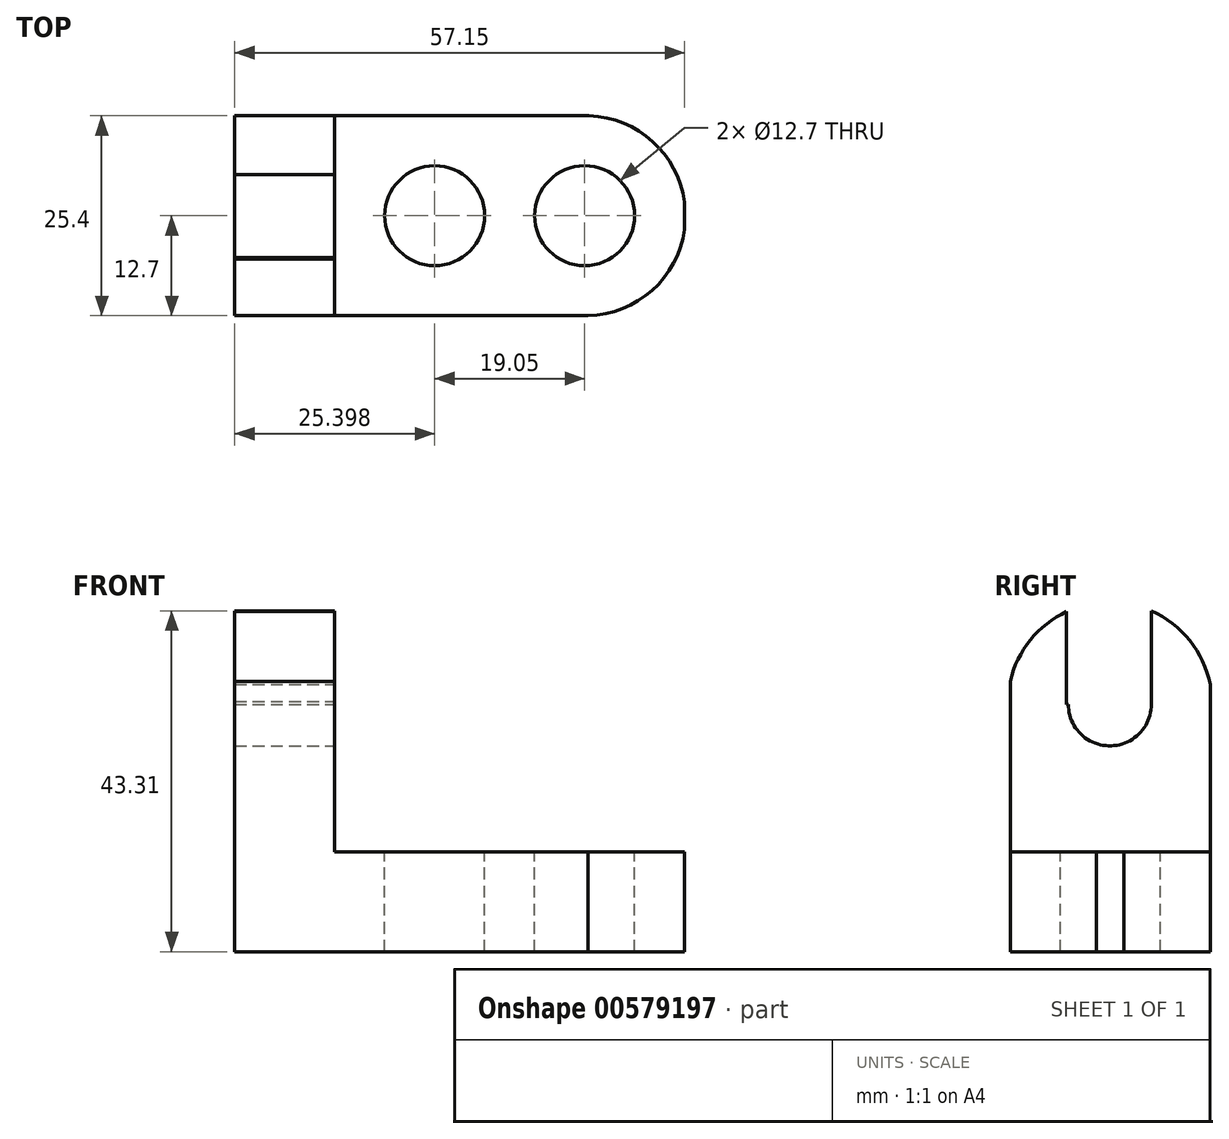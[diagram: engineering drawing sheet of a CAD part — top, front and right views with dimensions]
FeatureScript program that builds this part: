
annotation { "Feature Type Name" : "Feature", "Feature Type Description" : "" }
export const myFeature = defineFeature(function(context is Context, id is Id, definition is map)
    precondition{}
    {
        {
            var Q0;
            Q0=qCreatedBy(makeId("Front.planeOp"),FACE);
            var sketch = newSketch(context, id + "F0", { "sketchPlane" : qUnion([Q0])});
            skLineSegment(sketch, "E0", {"start": v(-58.37, 52.06) * mm, "end": v(-58.37, 7.61) * mm});
            skLineSegment(sketch, "E1", {"start": v(-58.37, 7.61) * mm, "end": v(-1.22, 7.61) * mm});
            skLineSegment(sketch, "E2", {"start": v(-1.22, 7.61) * mm, "end": v(-1.22, 20.31) * mm});
            skLineSegment(sketch, "E3", {"start": v(-1.22, 20.31) * mm, "end": v(-45.67, 20.31) * mm});
            skLineSegment(sketch, "E4", {"start": v(-45.67, 20.31) * mm, "end": v(-45.67, 52.06) * mm});
            skLineSegment(sketch, "E5", {"start": v(-45.67, 52.06) * mm, "end": v(-58.37, 52.06) * mm});
            skSolve(sketch);
        }
        {
            var Q0;
            Q0=makeQuery(id+"F0.imprint","IMPRINT",FACE,{"disambiguationData":[TD([[makeQuery(id+"F0.imprint","IMPRINT",EDGE,{"derivedFrom":sQuery(id+"F0.wireOp",EDGE,"E0")}),1.0]])]});
            extrude(context, id + "F1", {"entities" : qUnion([Q0]), "depth" : 25.4 * mm, "offsetDistance" : 25.4 * mm});
        }
        {
            var Q0;
            Q0=makeQuery(id+"F1.opExtrude","SWEPT_FACE",FACE,{"disambiguationData":[OSD([sQuery(id+"F0.wireOp",EDGE,"E3")])]});
            var sketch = newSketch(context, id + "F2", { "sketchPlane" : qUnion([Q0])});
            skCircle(sketch, "E6", {"center": v(-32.97, -12.7) * mm, "radius": 6.35 * mm});
            skCircle(sketch, "E7", {"center": v(-13.92, -12.7) * mm, "radius": 6.35 * mm});
            skSolve(sketch);
        }
        {
            var Q0;
            Q0=makeQuery(id+"F2.imprint","IMPRINT",FACE,{"disambiguationData":[TD([[makeQuery(id+"F2.imprint","IMPRINT",EDGE,{"derivedFrom":sQuery(id+"F2.wireOp",EDGE,"E6")}),1.0]])]});
            var Q1;
            Q1=makeQuery(id+"F2.imprint","IMPRINT",FACE,{"disambiguationData":[TD([[makeQuery(id+"F2.imprint","IMPRINT",EDGE,{"derivedFrom":sQuery(id+"F2.wireOp",EDGE,"E7")}),1.0]])]});
            extrude(context, id + "F3", {"entities" : qUnion([Q0, Q1]), "operationType" : NewBodyOperationType.REMOVE, "endBound" : BoundingType.THROUGH_ALL, "oppositeDirection" : true, "depth" : 25.4 * mm, "offsetDistance" : 25.4 * mm});
        }
        {
            var Q0;
            Q0=makeQuery(id+"F1.opExtrude","SWEPT_FACE",FACE,{"disambiguationData":[OSD([sQuery(id+"F0.wireOp",EDGE,"E3")])]});
            var sketch = newSketch(context, id + "F4", { "sketchPlane" : qUnion([Q0])});
            skArc(sketch, "E8", {"start": v(-14.1, -25.4) * mm, "mid": v(-1.1, -13.08) * mm, "end": v(-13.34, 0) * mm});
            skSolve(sketch);
        }
        {
            var Q0;
            {var subQ0=sQuery(id+"F4.wireOp",EDGE,"E8");var subQ1=sQuery(id+"F0.wireOp",EDGE,"E3");var subQ2=makeQuery(id+"F1.opExtrude","CAP_EDGE",EDGE,{"disambiguationData":[OSD([subQ1])],"isStart":true});var subQ3=makeQuery(id+"F4.imprint","INTERSECT",VERTEX,{"derivedFrom":[subQ2,subQ0]});Q0=makeQuery(id+"F4.imprint","IMPRINT",FACE,{"disambiguationData":[TD([[makeQuery(id+"F4.imprint","IMPRINT",EDGE,{"disambiguationData":[TD([[subQ3,1.0]])],"derivedFrom":subQ0}),-1.0]])]});}
            var Q1;
            {var subQ0=sQuery(id+"F4.wireOp",EDGE,"E8");var subQ1=sQuery(id+"F0.wireOp",EDGE,"E3");var subQ2=makeQuery(id+"F1.opExtrude","CAP_EDGE",EDGE,{"disambiguationData":[OSD([subQ1])],"isStart":false});var subQ3=makeQuery(id+"F4.imprint","INTERSECT",VERTEX,{"disambiguationData":[OD(1.0)],"derivedFrom":[subQ2,subQ0]});Q1=makeQuery(id+"F4.imprint","IMPRINT",FACE,{"disambiguationData":[TD([[makeQuery(id+"F4.imprint","IMPRINT",EDGE,{"disambiguationData":[TD([[subQ3,-1.0]])],"derivedFrom":subQ0}),-1.0]])]});}
            extrude(context, id + "F5", {"entities" : qUnion([Q0, Q1]), "operationType" : NewBodyOperationType.REMOVE, "endBound" : BoundingType.THROUGH_ALL, "oppositeDirection" : true, "depth" : 25.4 * mm, "offsetDistance" : 25.4 * mm});
        }
        {
            var Q0;
            Q0=makeQuery(id+"F1.opExtrude","SWEPT_FACE",FACE,{"disambiguationData":[OSD([sQuery(id+"F0.wireOp",EDGE,"E4")])]});
            var sketch = newSketch(context, id + "F6", { "sketchPlane" : qUnion([Q0])});
            skArc(sketch, "E9", {"start": v(0, 41.55) * mm, "mid": v(-12.53, 52.03) * mm, "end": v(-25.4, 41.97) * mm});
            skLineSegment(sketch, "E10", {"start": v(-18.24, 50.82) * mm, "end": v(-18.24, 39.05) * mm});
            skLineSegment(sketch, "E11", {"start": v(-18.24, 39.05) * mm, "end": v(-7.48, 39.05) * mm});
            skLineSegment(sketch, "E12", {"start": v(-7.48, 39.05) * mm, "end": v(-7.48, 50.92) * mm});
            skCircle(sketch, "E13", {"center": v(-12.75, 39.05) * mm, "radius": 5.28 * mm});
            skSolve(sketch);
        }
        {
            var Q0;
            {var subQ6=sQuery(id+"F6.wireOp",EDGE,"E10");Q0=makeQuery(id+"F6.imprint","IMPRINT",FACE,{"disambiguationData":[TD([[makeQuery(id+"F6.imprint","IMPRINT",EDGE,{"derivedFrom":subQ6}),1.0]])]});}
            var Q1;
            {var subQ1=sQuery(id+"F0.wireOp",EDGE,"E4");var subQ6=makeQuery(id+"F1.opExtrude","SWEPT_EDGE",EDGE,{"disambiguationData":[OSD([subQ1,sQuery(id+"F0.wireOp",EDGE,"E5")])]});Q1=makeQuery(id+"F6.imprint","IMPRINT",FACE,{"disambiguationData":[TD([[makeQuery(id+"F6.imprint","IMPRINT",EDGE,{"derivedFrom":subQ6}),-1.0]])]});}
            var Q2;
            {var subQ0=sQuery(id+"F6.wireOp",EDGE,"E12");var subQ1=sQuery(id+"F6.wireOp",EDGE,"E11");var subQ2=makeQuery(id+"F6.imprint","INTERSECT",VERTEX,{"derivedFrom":[subQ1,subQ0]});Q2=makeQuery(id+"F6.imprint","IMPRINT",FACE,{"disambiguationData":[TD([[makeQuery(id+"F6.imprint","IMPRINT",EDGE,{"disambiguationData":[TD([[subQ2,1.0]])],"derivedFrom":subQ1}),1.0]])]});}
            var Q3;
            {var subQ0=sQuery(id+"F6.wireOp",EDGE,"E12");var subQ1=sQuery(id+"F6.wireOp",EDGE,"E11");var subQ2=makeQuery(id+"F6.imprint","INTERSECT",VERTEX,{"derivedFrom":[subQ1,subQ0]});Q3=makeQuery(id+"F6.imprint","IMPRINT",FACE,{"disambiguationData":[TD([[makeQuery(id+"F6.imprint","IMPRINT",EDGE,{"disambiguationData":[TD([[subQ2,1.0]])],"derivedFrom":subQ1}),-1.0]])]});}
            extrude(context, id + "F7", {"entities" : qUnion([Q0, Q1, Q2, Q3]), "operationType" : NewBodyOperationType.REMOVE, "endBound" : BoundingType.THROUGH_ALL, "oppositeDirection" : true, "depth" : 25.4 * mm, "offsetDistance" : 25.4 * mm});
        }
    });
